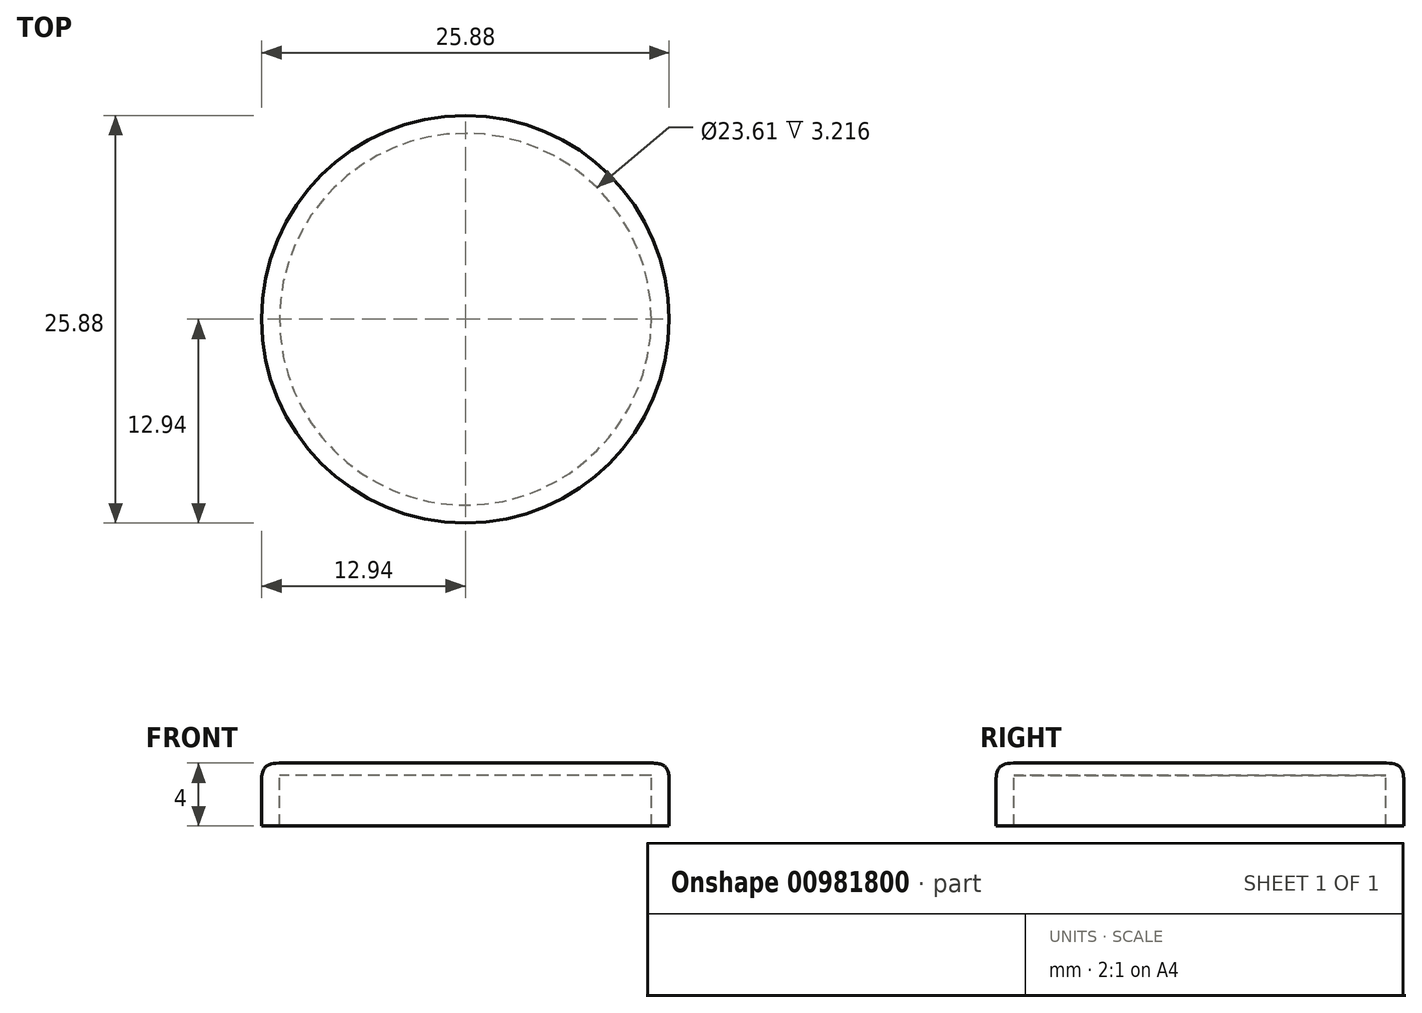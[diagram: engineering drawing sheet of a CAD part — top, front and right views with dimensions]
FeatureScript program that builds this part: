
annotation { "Feature Type Name" : "Feature", "Feature Type Description" : "" }
export const myFeature = defineFeature(function(context is Context, id is Id, definition is map)
    precondition{}
    {
        {
            var Q0;
            Q0=qCreatedBy(makeId("Front.planeOp"),FACE);
            var sketch = newSketch(context, id + "F0", { "sketchPlane" : qUnion([Q0])});
            skLineSegment(sketch, "E0", {"start": v(0, 0) * mm, "end": v(12.94, 0) * mm});
            skLineSegment(sketch, "E1", {"start": v(12.94, 0) * mm, "end": v(12.94, 4) * mm});
            skLineSegment(sketch, "E2", {"start": v(12.94, 4) * mm, "end": v(0, 4) * mm});
            skLineSegment(sketch, "E3", {"start": v(0, 4) * mm, "end": v(0, 0) * mm});
            skLineSegment(sketch, "E4", {"start": v(0, 6.9) * mm, "end": v(0, -2.53) * mm});
            skLineSegment(sketch, "E5.bottom", {"start": v(0, 3.22) * mm, "end": v(11.8, 3.22) * mm});
            skLineSegment(sketch, "E5.top", {"start": v(0, 0) * mm, "end": v(11.8, 0) * mm});
            skLineSegment(sketch, "E5.left", {"start": v(0, 3.22) * mm, "end": v(0, 0) * mm});
            skLineSegment(sketch, "E5.right", {"start": v(11.8, 3.22) * mm, "end": v(11.8, 0) * mm});
            skFitSpline(sketch, "E6", {"points": [v(11.68, 4) * mm, v(12.94, 2.9) * mm], "startDerivative": vector(2.78, 0) * mm, "endDerivative": vector(0, -2.7) * mm});
            skFitSpline(sketch, "E7", {"points": [v(11.24, 3.22) * mm, v(11.8, 2.7) * mm], "startDerivative": vector(1.14, 0) * mm, "endDerivative": vector(0, -1.32) * mm});
            skSolve(sketch);
        }
        {
            var Q0;
            {var subQ0=sQuery(id+"F0.wireOp",EDGE,"E6");Q0=makeQuery(id+"F0.imprint","IMPRINT",FACE,{"disambiguationData":[TD([[makeQuery(id+"F0.imprint","IMPRINT",EDGE,{"derivedFrom":subQ0}),-1.0]])]});}
            var Q1;
            Q1=sQuery(id+"F0.wireOp",EDGE,"E4");
            revolve(context, id + "F1", {"surfaceOperationType" : NewSurfaceOperationType.NEW, "entities" : qUnion([Q0]), "axis" : qUnion([Q1]), "revolveType" : RevolveType.FULL});
        }
    });
